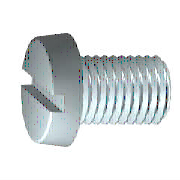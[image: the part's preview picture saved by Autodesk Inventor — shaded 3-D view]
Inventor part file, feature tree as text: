
AUTODESK INVENTOR PART (.ipt)
format: ipt  version: 2023.2 (Build 272271030, 271C)  size: 186,880 bytes
history: native  units: mm (DEFAULTED — no unit token found)
features: sketch x2, extrude x1, plane x1
ambient origin geometry x7: Origin, YZ Plane, XZ Plane, X Axis, Y Axis, Z Axis, Center Point
bodies: Solid1 (feature_tree), Body (feature_tree)
feature tree (4):
  sketch  "Sketch2"  dims[d2=0.766912mm d3=5.0mm d4=8.0mm d5=7.323417mm d8=90.0deg d7=0.0mm d9=13.0mm d10=0.872665mm d11=2.0mm d12=13.0mm d14=0.4mm d15=7.5mm d16=0.0mm d17=0.67658mm d18=0.766912mm d19=2.0mm d20=0.0mm d36=45.0deg d37=0.0mm d39=0.0mm]
  extrude  "Slot"  Depth=10.0mm
  plane  "Work Plane1"
  sketch  "Sketch1"  dims[d0=10.0mm d1=7.5mm]
